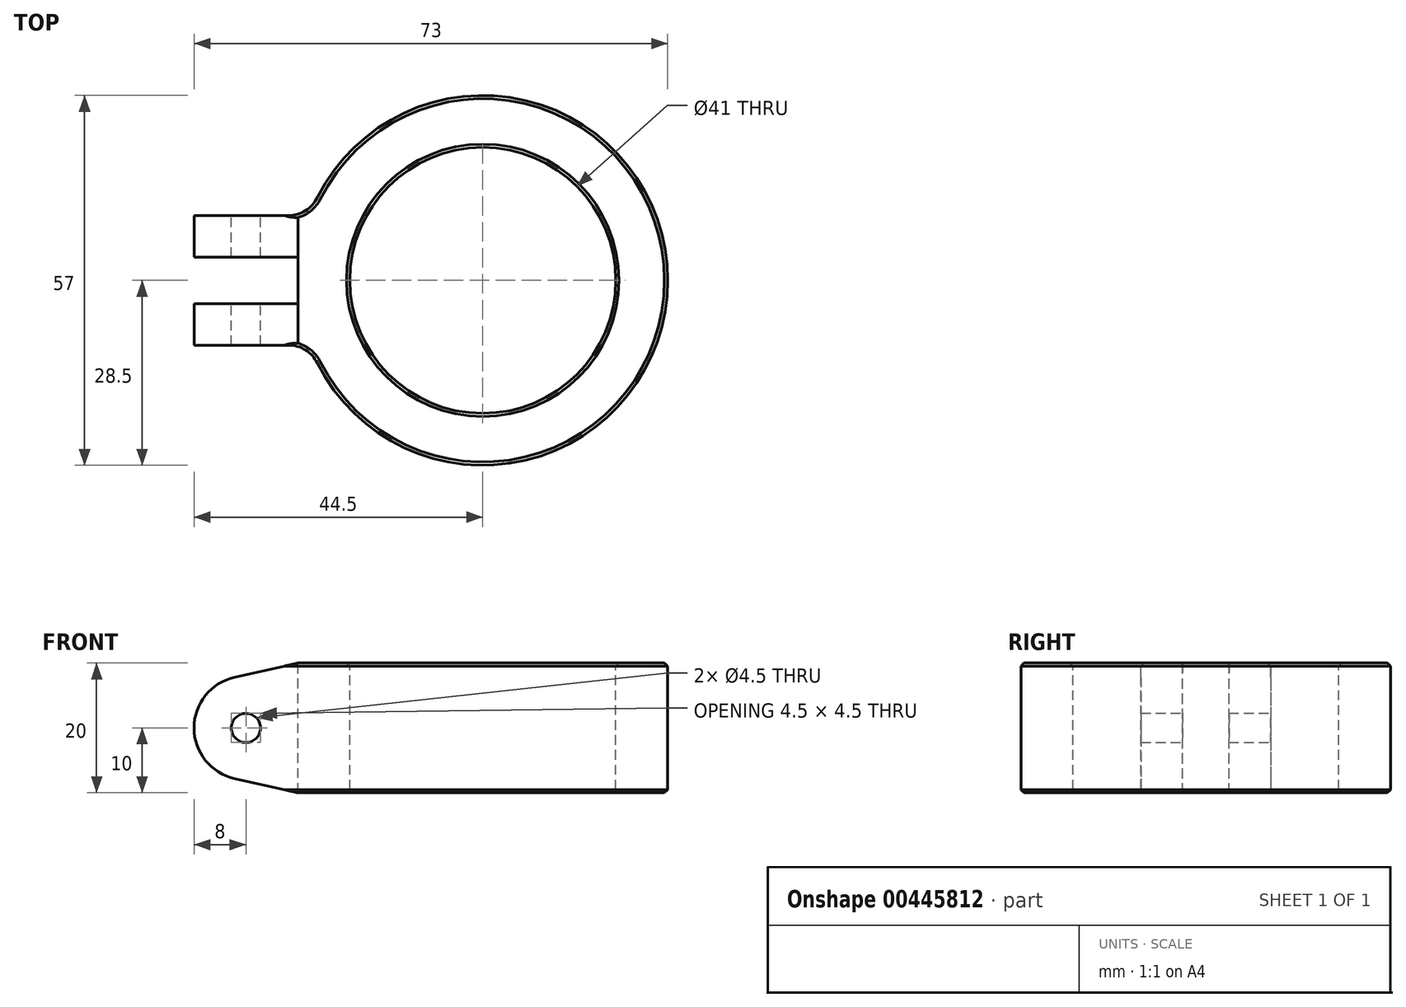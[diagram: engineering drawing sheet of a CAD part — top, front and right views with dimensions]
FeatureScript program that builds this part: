
annotation { "Feature Type Name" : "Feature", "Feature Type Description" : "" }
export const myFeature = defineFeature(function(context is Context, id is Id, definition is map)
    precondition{}
    {
        {
            var Q0;
            Q0=qCreatedBy(makeId("Front.planeOp"),FACE);
            var sketch = newSketch(context, id + "F0", { "sketchPlane" : qUnion([Q0])});
            skLineSegment(sketch, "E0", {"start": v(0, 164.32) * mm, "end": v(0, -116.58) * mm, "construction": true});
            skLineSegment(sketch, "E1", {"start": v(-20.5, 20) * mm, "end": v(-20.5, 0) * mm});
            skLineSegment(sketch, "E2", {"start": v(-28.5, 20) * mm, "end": v(-20.5, 20) * mm});
            skLineSegment(sketch, "E3", {"start": v(-28.5, 0) * mm, "end": v(-20.5, 0) * mm});
            skLineSegment(sketch, "E4", {"start": v(-28.5, 0) * mm, "end": v(-28.5, 20) * mm});
            skLineSegment(sketch, "E5", {"start": v(-28.5, 10) * mm, "end": v(-59.56, 10) * mm, "construction": true});
            skPoint(sketch, "E5.endSnap0", {"position": v(-28.5, 10) * mm});
            skCircle(sketch, "E6", {"center": v(-36.5, 10) * mm, "radius": 8 * mm});
            skLineSegment(sketch, "E7", {"start": v(-38.26, 17.8) * mm, "end": v(-28.5, 20) * mm});
            skLineSegment(sketch, "E8", {"start": v(-38.26, 2.2) * mm, "end": v(-28.5, 0) * mm});
            skCircle(sketch, "E9", {"center": v(-36.5, 10) * mm, "radius": 2.25 * mm});
            skSolve(sketch);
        }
        {
            var Q0;
            Q0=makeQuery(id+"F0.imprint","IMPRINT",FACE,{"disambiguationData":[TD([[makeQuery(id+"F0.imprint","IMPRINT",EDGE,{"derivedFrom":sQuery(id+"F0.wireOp",EDGE,"E1")}),-1.0]])]});
            var Q1;
            Q1=sQuery(id+"F0.wireOp",EDGE,"E0");
            revolve(context, id + "F1", {"entities" : qUnion([Q0]), "axis" : qUnion([Q1]), "revolveType" : RevolveType.FULL});
        }
        {
            var Q0;
            Q0=makeQuery(id+"F0.imprint","IMPRINT",FACE,{"disambiguationData":[TD([[makeQuery(id+"F0.imprint","IMPRINT",EDGE,{"derivedFrom":sQuery(id+"F0.wireOp",EDGE,"E1")}),-1.0]])]});
            var Q1;
            {var subQ0=sQuery(id+"F0.wireOp",EDGE,"E7");Q1=makeQuery(id+"F0.imprint","IMPRINT",FACE,{"disambiguationData":[TD([[makeQuery(id+"F0.imprint","IMPRINT",EDGE,{"derivedFrom":subQ0}),-1.0]])]});}
            var Q2;
            {var subQ0=sQuery(id+"F0.wireOp",EDGE,"E8");Q2=makeQuery(id+"F0.imprint","IMPRINT",FACE,{"disambiguationData":[TD([[makeQuery(id+"F0.imprint","IMPRINT",EDGE,{"derivedFrom":subQ0}),1.0]])]});}
            var Q3;
            Q3=makeQuery(id+"F0.imprint","IMPRINT",FACE,{"disambiguationData":[TD([[makeQuery(id+"F0.imprint","IMPRINT",EDGE,{"derivedFrom":sQuery(id+"F0.wireOp",EDGE,"E9")}),-1.0]])]});
            extrude(context, id + "F2", {"entities" : qUnion([Q0, Q1, Q2, Q3]), "operationType" : NewBodyOperationType.ADD, "endBound" : BoundingType.SYMMETRIC, "depth" : 20 * mm, "offsetDistance" : 25 * mm});
        }
        {
            var Q0;
            Q0=makeQuery(id+"F2.opExtrude","SWEPT_FACE",FACE,{"disambiguationData":[OSD([sQuery(id+"F0.wireOp",EDGE,"E2")])]});
            var sketch = newSketch(context, id + "F3", { "sketchPlane" : qUnion([Q0])});
            skLineSegment(sketch, "E10.bottom", {"start": v(-28.5, 3.58) * mm, "end": v(-44.5, 3.58) * mm});
            skLineSegment(sketch, "E10.top", {"start": v(-28.5, -3.58) * mm, "end": v(-44.5, -3.58) * mm});
            skLineSegment(sketch, "E10.left", {"start": v(-28.5, -3.58) * mm, "end": v(-28.5, 3.58) * mm});
            skLineSegment(sketch, "E10.right", {"start": v(-44.5, -3.58) * mm, "end": v(-44.5, 3.58) * mm});
            skPoint(sketch, "E11", {"position": v(-28.5, 0) * mm});
            skSolve(sketch);
        }
        {
            var Q0;
            Q0=makeQuery(id+"F3.imprint","IMPRINT",FACE,{"disambiguationData":[TD([[makeQuery(id+"F3.imprint","IMPRINT",EDGE,{"derivedFrom":sQuery(id+"F3.wireOp",EDGE,"E10.bottom")}),1.0]])]});
            extrude(context, id + "F4", {"entities" : qUnion([Q0]), "operationType" : NewBodyOperationType.REMOVE, "endBound" : BoundingType.THROUGH_ALL, "oppositeDirection" : true, "depth" : 25 * mm, "offsetDistance" : 25 * mm});
        }
        {
            var Q0;
            Q0=makeQuery(id+"F2.boolean.opBoolean","INTERSECT",EDGE,{"derivedFrom":[makeQuery(id+"F1.opRevolve","SWEPT_FACE",FACE,{"disambiguationData":[OSD([sQuery(id+"F0.wireOp",EDGE,"E4")])]}),makeQuery(id+"F2.opExtrude","CAP_FACE",FACE,{"disambiguationData":[OSD([sQuery(id+"F0.wireOp",EDGE,"E1"),sQuery(id+"F0.wireOp",EDGE,"E2"),sQuery(id+"F0.wireOp",EDGE,"E3"),sQuery(id+"F0.wireOp",EDGE,"E6"),sQuery(id+"F0.wireOp",EDGE,"E7"),sQuery(id+"F0.wireOp",EDGE,"E8"),sQuery(id+"F0.wireOp",EDGE,"E9")])],"isStart":true})]});
            var Q1;
            Q1=makeQuery(id+"F2.boolean.opBoolean","INTERSECT",EDGE,{"derivedFrom":[makeQuery(id+"F1.opRevolve","SWEPT_FACE",FACE,{"disambiguationData":[OSD([sQuery(id+"F0.wireOp",EDGE,"E4")])]}),makeQuery(id+"F2.opExtrude","CAP_FACE",FACE,{"disambiguationData":[OSD([sQuery(id+"F0.wireOp",EDGE,"E1"),sQuery(id+"F0.wireOp",EDGE,"E2"),sQuery(id+"F0.wireOp",EDGE,"E3"),sQuery(id+"F0.wireOp",EDGE,"E6"),sQuery(id+"F0.wireOp",EDGE,"E7"),sQuery(id+"F0.wireOp",EDGE,"E8"),sQuery(id+"F0.wireOp",EDGE,"E9")])],"isStart":false})]});
            fillet(context, id + "F5", {"entities" : qUnion([Q0, Q1]), "radius" : 5 * mm, "tangentPropagation" : true, "allowEdgeOverflow" : false});
        }
        {
            var Q0;
            Q0=makeQuery(id+"F1.opRevolve","SWEPT_EDGE",EDGE,{"disambiguationData":[OSD([sQuery(id+"F0.wireOp",EDGE,"E3"),sQuery(id+"F0.wireOp",EDGE,"E4"),sQuery(id+"F0.wireOp",EDGE,"E8")])]});
            var Q1;
            Q1=makeQuery(id+"F1.opRevolve","SWEPT_EDGE",EDGE,{"disambiguationData":[OSD([sQuery(id+"F0.wireOp",EDGE,"E2"),sQuery(id+"F0.wireOp",EDGE,"E4"),sQuery(id+"F0.wireOp",EDGE,"E7")])]});
            var Q2;
            Q2=makeQuery(id+"F1.opRevolve","SWEPT_EDGE",EDGE,{"disambiguationData":[OSD([sQuery(id+"F0.wireOp",EDGE,"E1"),sQuery(id+"F0.wireOp",EDGE,"E2")])]});
            var Q3;
            Q3=makeQuery(id+"F1.opRevolve","SWEPT_EDGE",EDGE,{"disambiguationData":[OSD([sQuery(id+"F0.wireOp",EDGE,"E1"),sQuery(id+"F0.wireOp",EDGE,"E3")])]});
            chamfer(context, id + "F6", {"entities" : qUnion([Q0, Q1, Q2, Q3]), "width" : 0.5 * mm, "tangentPropagation" : true});
        }
    });
